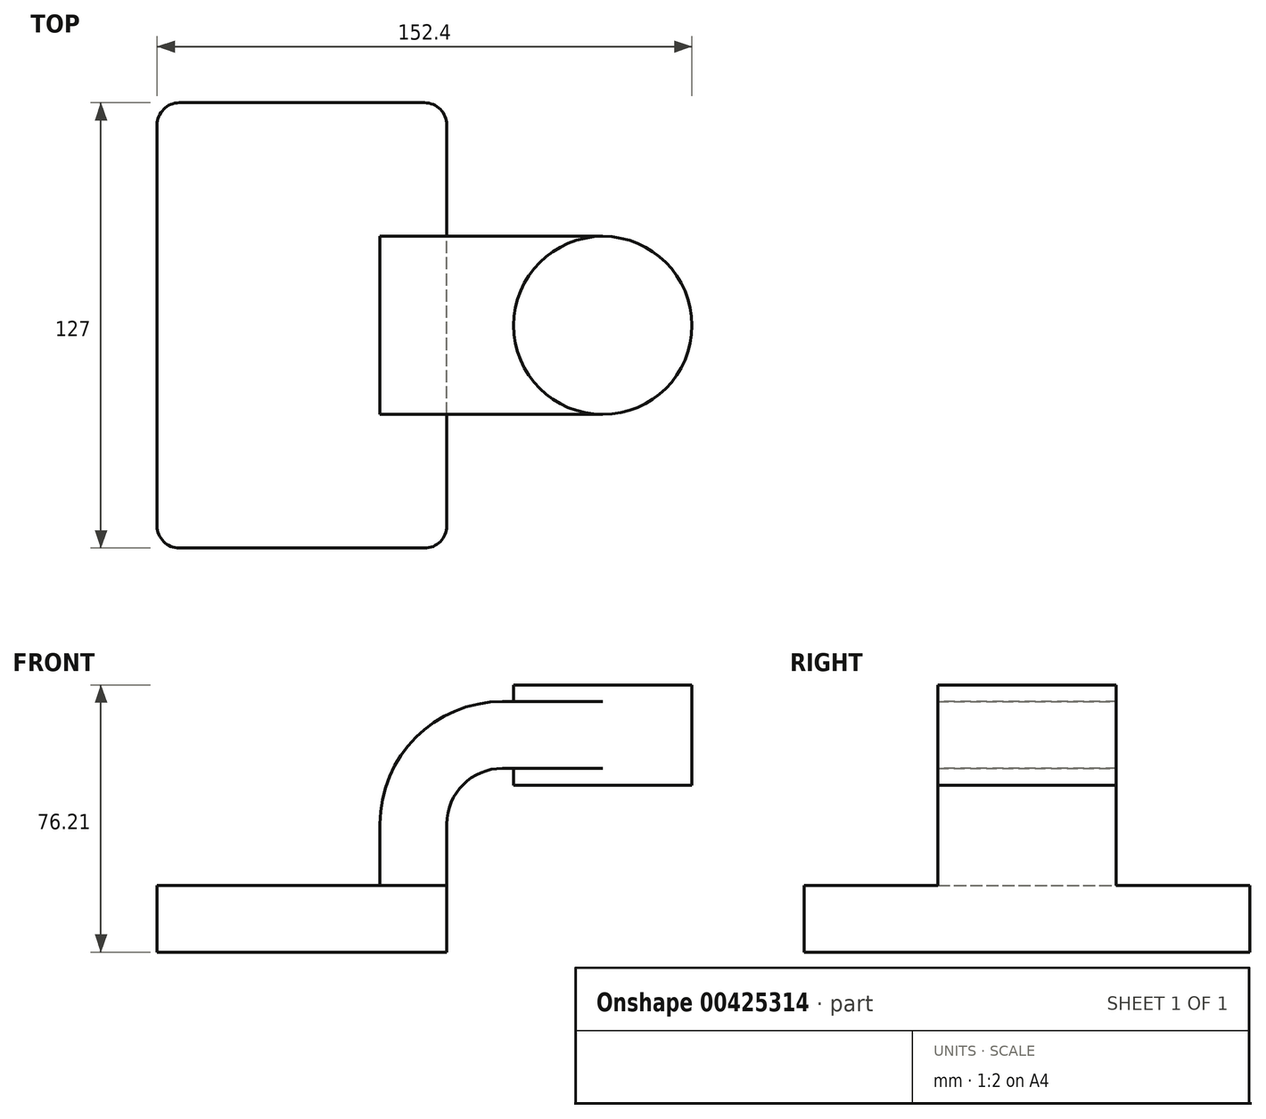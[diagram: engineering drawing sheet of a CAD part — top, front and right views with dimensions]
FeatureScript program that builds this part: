
annotation { "Feature Type Name" : "Feature", "Feature Type Description" : "" }
export const myFeature = defineFeature(function(context is Context, id is Id, definition is map)
    precondition{}
    {
        {
            var Q0;
            Q0=qCreatedBy(makeId("Front.planeOp"),FACE);
            var sketch = newSketch(context, id + "F0", { "sketchPlane" : qUnion([Q0])});
            skLineSegment(sketch, "E0.bottom", {"start": v(41.27, 9.53) * mm, "end": v(-41.28, 9.53) * mm});
            skLineSegment(sketch, "E0.top", {"start": v(41.28, -9.52) * mm, "end": v(-41.27, -9.52) * mm});
            skLineSegment(sketch, "E0.left", {"start": v(41.27, 9.53) * mm, "end": v(41.28, -9.52) * mm});
            skLineSegment(sketch, "E0.right", {"start": v(-41.28, 9.53) * mm, "end": v(-41.27, -9.52) * mm});
            skPoint(sketch, "E0.middle", {"position": v(0, 0) * mm});
            skLineSegment(sketch, "E1.bottom", {"start": v(60.32, 38.1) * mm, "end": v(111.12, 38.1) * mm});
            skLineSegment(sketch, "E1.top", {"start": v(60.32, 66.68) * mm, "end": v(111.12, 66.68) * mm});
            skLineSegment(sketch, "E1.left", {"start": v(60.32, 38.1) * mm, "end": v(60.32, 66.68) * mm});
            skLineSegment(sketch, "E1.right", {"start": v(111.12, 38.1) * mm, "end": v(111.12, 66.68) * mm});
            skPoint(sketch, "E1.middle", {"position": v(85.72, 52.39) * mm});
            skLineSegment(sketch, "E2", {"start": v(41.27, 9.53) * mm, "end": v(41.27, 27) * mm});
            skArc(sketch, "E3", {"start": v(41.27, 27) * mm, "mid": v(45.92, 38.23) * mm, "end": v(57.15, 42.88) * mm});
            skLineSegment(sketch, "E4", {"start": v(57.15, 42.88) * mm, "end": v(85.72, 42.88) * mm});
            skLineSegment(sketch, "E5", {"start": v(85.72, 52.39) * mm, "end": v(85.72, 42.88) * mm, "construction": true});
            skLineSegment(sketch, "E6.0", {"start": v(57.15, 61.93) * mm, "end": v(85.72, 61.93) * mm});
            skArc(sketch, "E6.1", {"start": v(22.22, 27) * mm, "mid": v(32.45, 51.7) * mm, "end": v(57.15, 61.93) * mm});
            skLineSegment(sketch, "E6.2", {"start": v(22.22, 9.53) * mm, "end": v(22.22, 27) * mm});
            skLineSegment(sketch, "E7", {"start": v(85.72, 66.68) * mm, "end": v(85.72, 38.1) * mm});
            skFitSpline(sketch, "E8", {"points": [v(-41.28, 9.52) * mm, v(57.15, 61.93) * mm], "startDerivative": vector(0.32, 114.63) * mm, "endDerivative": vector(130.72, -3.42) * mm});
            skSolve(sketch);
        }
        {
            var Q0;
            Q0=makeQuery(id+"F0.imprint","IMPRINT",FACE,{"disambiguationData":[TD([[makeQuery(id+"F0.imprint","IMPRINT",EDGE,{"derivedFrom":sQuery(id+"F0.wireOp",EDGE,"E0.top")}),-1.0]])]});
            extrude(context, id + "F1", {"entities" : qUnion([Q0]), "endBound" : BoundingType.SYMMETRIC, "depth" : 127 * mm});
        }
        {
            var Q0;
            {var subQ1=sQuery(id+"F0.wireOp",EDGE,"E2");Q0=makeQuery(id+"F0.imprint","IMPRINT",FACE,{"disambiguationData":[TD([[makeQuery(id+"F0.imprint","IMPRINT",EDGE,{"derivedFrom":subQ1}),1.0]])]});}
            var Q1;
            {var subQ0=sQuery(id+"F0.wireOp",EDGE,"E4");var subQ1=sQuery(id+"F0.wireOp",EDGE,"E1.left");var subQ2=makeQuery(id+"F0.imprint","INTERSECT",VERTEX,{"derivedFrom":[subQ1,subQ0]});Q1=makeQuery(id+"F0.imprint","IMPRINT",FACE,{"disambiguationData":[TD([[makeQuery(id+"F0.imprint","IMPRINT",EDGE,{"disambiguationData":[TD([[subQ2,-1.0]])],"derivedFrom":subQ1}),-1.0]])]});}
            extrude(context, id + "F2", {"entities" : qUnion([Q0, Q1]), "operationType" : NewBodyOperationType.ADD, "endBound" : BoundingType.SYMMETRIC, "depth" : 50.8 * mm});
        }
        {
            var Q0;
            Q0=makeQuery(id+"F0.imprint","IMPRINT",FACE,{"disambiguationData":[TD([[makeQuery(id+"F0.imprint","IMPRINT",EDGE,{"derivedFrom":sQuery(id+"F0.wireOp",EDGE,"E6.1")}),1.0]])]});
            extrude(context, id + "F3", {"entities" : qUnion([Q0]), "operationType" : NewBodyOperationType.ADD, "endBound" : BoundingType.SYMMETRIC, "depth" : 15.88 * mm});
        }
        {
            var Q0;
            {var subQ0=sQuery(id+"F0.wireOp",EDGE,"E1.right");Q0=makeQuery(id+"F0.imprint","IMPRINT",FACE,{"disambiguationData":[TD([[makeQuery(id+"F0.imprint","IMPRINT",EDGE,{"derivedFrom":subQ0}),1.0]])]});}
            var Q1;
            Q1=sQuery(id+"F0.wireOp",EDGE,"E7");
            revolve(context, id + "F4", {"operationType" : NewBodyOperationType.ADD, "entities" : qUnion([Q0]), "axis" : qUnion([Q1]), "revolveType" : RevolveType.FULL});
        }
        {
            var Q0;
            Q0=makeQuery(id+"F1.opExtrude","CAP_EDGE",EDGE,{"disambiguationData":[OSD([sQuery(id+"F0.wireOp",EDGE,"E0.left")])],"isStart":false});
            var Q1;
            Q1=makeQuery(id+"F1.opExtrude","CAP_EDGE",EDGE,{"disambiguationData":[OSD([sQuery(id+"F0.wireOp",EDGE,"E0.right")])],"isStart":false});
            var Q2;
            Q2=makeQuery(id+"F1.opExtrude","CAP_EDGE",EDGE,{"disambiguationData":[OSD([sQuery(id+"F0.wireOp",EDGE,"E0.left")])],"isStart":true});
            var Q3;
            Q3=makeQuery(id+"F1.opExtrude","CAP_EDGE",EDGE,{"disambiguationData":[OSD([sQuery(id+"F0.wireOp",EDGE,"E0.right")])],"isStart":true});
            fillet(context, id + "F5", {"entities" : qUnion([Q0, Q1, Q2, Q3]), "radius" : 6.35 * mm, "tangentPropagation" : true, "allowEdgeOverflow" : false});
        }
    });
